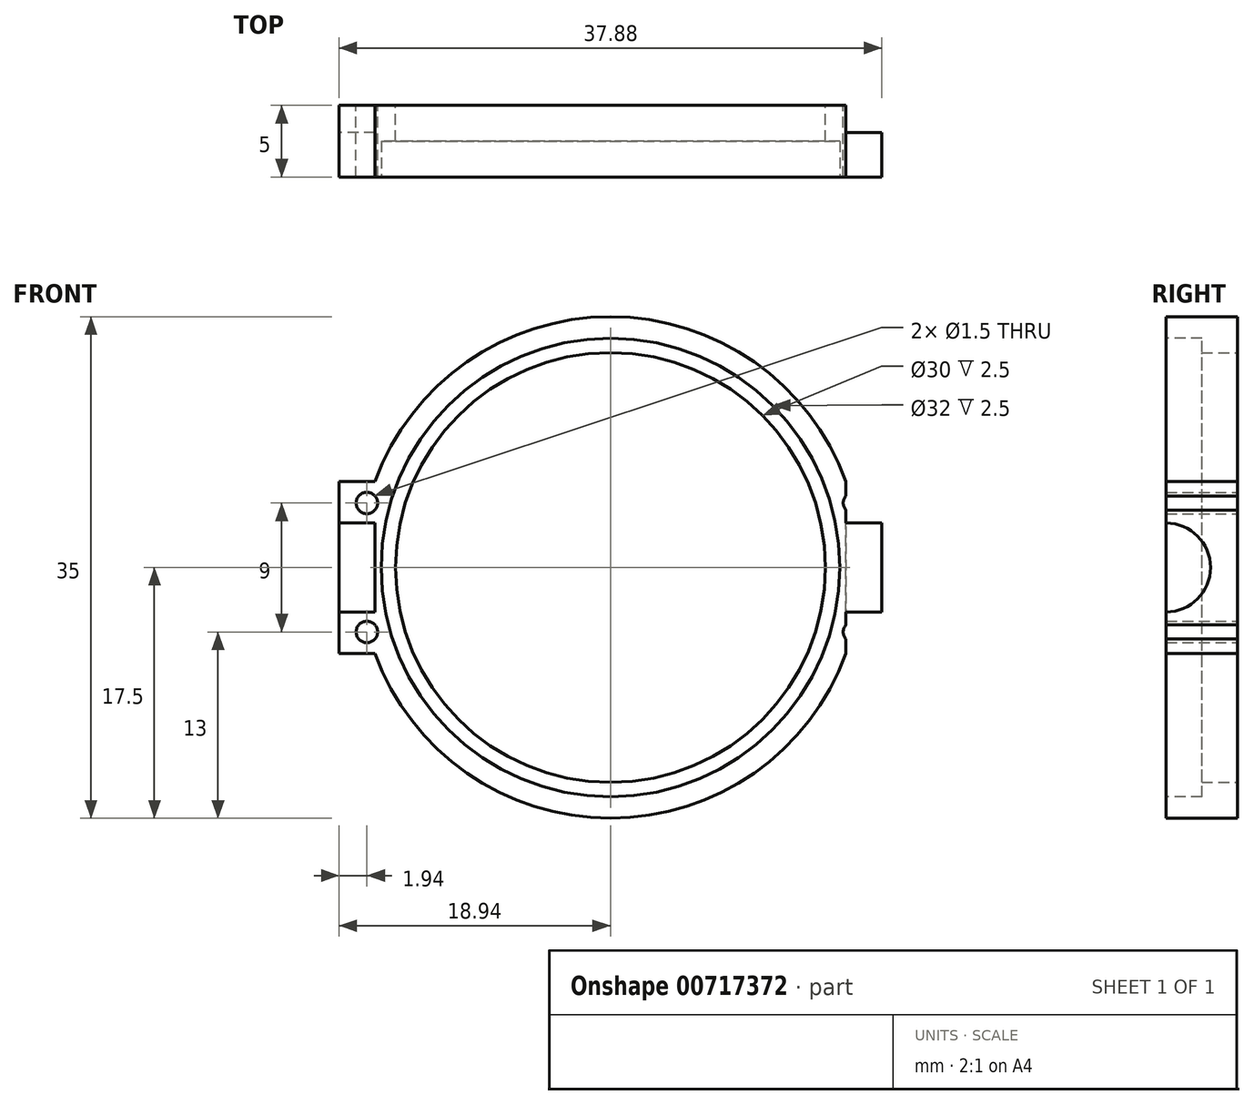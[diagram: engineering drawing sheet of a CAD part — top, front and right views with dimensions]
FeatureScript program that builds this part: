
annotation { "Feature Type Name" : "Feature", "Feature Type Description" : "" }
export const myFeature = defineFeature(function(context is Context, id is Id, definition is map)
    precondition{}
    {
        {
            var Q0;
            Q0=qCreatedBy(makeId("Front.planeOp"),FACE);
            var sketch = newSketch(context, id + "F0", { "sketchPlane" : qUnion([Q0])});
            skCircle(sketch, "E0", {"center": v(0, 0) * mm, "radius": 15 * mm});
            skArc(sketch, "E1", {"start": v(-16.44, -6) * mm, "mid": v(0, -17.5) * mm, "end": v(16.44, -6) * mm});
            skLineSegment(sketch, "E2.bottom", {"start": v(-16.44, 6) * mm, "end": v(-18.94, 6) * mm});
            skLineSegment(sketch, "E2.top", {"start": v(-16.44, -6) * mm, "end": v(-18.94, -6) * mm});
            skLineSegment(sketch, "E2.right", {"start": v(-18.94, 6) * mm, "end": v(-18.94, -6) * mm});
            skLineSegment(sketch, "E3.MirrorCS", {"start": v(16.44, -6) * mm, "end": v(18.94, -6) * mm});
            skLineSegment(sketch, "E4.MirrorCS", {"start": v(16.44, 6) * mm, "end": v(18.94, 6) * mm});
            skLineSegment(sketch, "E5.MirrorCS", {"start": v(18.94, 6) * mm, "end": v(18.94, -6) * mm});
            skArc(sketch, "E6.trimOffspring", {"start": v(16.44, 6) * mm, "mid": v(0, 17.5) * mm, "end": v(-16.44, 6) * mm});
            skSolve(sketch);
        }
        {
            var Q0;
            Q0=makeQuery(id+"F0.imprint","IMPRINT",FACE,{"disambiguationData":[TD([[makeQuery(id+"F0.imprint","IMPRINT",EDGE,{"derivedFrom":sQuery(id+"F0.wireOp",EDGE,"E0")}),-1.0]])]});
            extrude(context, id + "F1", {"entities" : qUnion([Q0]), "depth" : 5 * mm, "offsetDistance" : 25 * mm});
        }
        {
            var Q0;
            Q0=makeQuery(id+"F1.opExtrude","CAP_FACE",FACE,{"disambiguationData":[OSD([sQuery(id+"F0.wireOp",EDGE,"E0"),sQuery(id+"F0.wireOp",EDGE,"E1"),sQuery(id+"F0.wireOp",EDGE,"E2.bottom"),sQuery(id+"F0.wireOp",EDGE,"E2.top"),sQuery(id+"F0.wireOp",EDGE,"E2.right"),sQuery(id+"F0.wireOp",EDGE,"E3.MirrorCS"),sQuery(id+"F0.wireOp",EDGE,"E4.MirrorCS"),sQuery(id+"F0.wireOp",EDGE,"E5.MirrorCS"),sQuery(id+"F0.wireOp",EDGE,"E6.trimOffspring")])],"isStart":false});
            var sketch = newSketch(context, id + "F2", { "sketchPlane" : qUnion([Q0])});
            skCircle(sketch, "E7.0", {"center": v(0, 0) * mm, "radius": 15 * mm});
            skCircle(sketch, "E8.0", {"center": v(0, 0) * mm, "radius": 16 * mm});
            skSolve(sketch);
        }
        {
            var Q0;
            Q0=makeQuery(id+"F2.imprint","IMPRINT",FACE,{"disambiguationData":[TD([[makeQuery(id+"F2.imprint","IMPRINT",EDGE,{"derivedFrom":sQuery(id+"F2.wireOp",EDGE,"E7.0")}),-1.0]])]});
            extrude(context, id + "F3", {"entities" : qUnion([Q0]), "operationType" : NewBodyOperationType.REMOVE, "oppositeDirection" : true, "depth" : 2.5 * mm, "offsetDistance" : 25 * mm});
        }
        {
            var Q0;
            Q0=makeQuery(id+"F1.opExtrude","SWEPT_FACE",FACE,{"disambiguationData":[OSD([sQuery(id+"F0.wireOp",EDGE,"E2.right")])]});
            var sketch = newSketch(context, id + "F4", { "sketchPlane" : qUnion([Q0])});
            skArc(sketch, "E9", {"start": v(5, 3.1) * mm, "mid": v(1.9, 0) * mm, "end": v(5, -3.1) * mm});
            skLineSegment(sketch, "E10", {"start": v(5, 3.1) * mm, "end": v(5, -3.1) * mm});
            skSolve(sketch);
        }
        {
            var Q0;
            Q0=makeQuery(id+"F4.imprint","IMPRINT",FACE,{"disambiguationData":[TD([[makeQuery(id+"F4.imprint","IMPRINT",EDGE,{"derivedFrom":sQuery(id+"F4.wireOp",EDGE,"E9")}),1.0]])]});
            extrude(context, id + "F5", {"entities" : qUnion([Q0]), "operationType" : NewBodyOperationType.REMOVE, "oppositeDirection" : true, "depth" : 2.5 * mm, "offsetDistance" : 25 * mm});
        }
        {
            var Q0;
            Q0=makeQuery(id+"F1.opExtrude","SWEPT_FACE",FACE,{"disambiguationData":[OSD([sQuery(id+"F0.wireOp",EDGE,"E5.MirrorCS")])]});
            var sketch = newSketch(context, id + "F6", { "sketchPlane" : qUnion([Q0])});
            skArc(sketch, "E11", {"start": v(-5, 3.1) * mm, "mid": v(-1.9, 0) * mm, "end": v(-5, -3.1) * mm});
            skLineSegment(sketch, "E12", {"start": v(-5, 3.1) * mm, "end": v(-5, -3.1) * mm});
            skSolve(sketch);
        }
        {
            var Q0;
            Q0=makeQuery(id+"F6.imprint","IMPRINT",FACE,{"disambiguationData":[TD([[makeQuery(id+"F6.imprint","IMPRINT",EDGE,{"derivedFrom":sQuery(id+"F6.wireOp",EDGE,"E11")}),-1.0]])]});
            extrude(context, id + "F7", {"entities" : qUnion([Q0]), "operationType" : NewBodyOperationType.REMOVE, "oppositeDirection" : true, "depth" : 2.5 * mm, "offsetDistance" : 25 * mm});
        }
        {
            var Q0;
            Q0=qCreatedBy(makeId("Front.planeOp"),FACE);
            var sketch = newSketch(context, id + "F8", { "sketchPlane" : qUnion([Q0])});
            skPoint(sketch, "E13", {"position": v(-17, 4.5) * mm});
            skPoint(sketch, "E14", {"position": v(-17, -4.5) * mm});
            skPoint(sketch, "E15.MirrorP", {"position": v(17, 4.5) * mm});
            skPoint(sketch, "E16.MirrorP", {"position": v(17, -4.5) * mm});
            skSolve(sketch);
        }
        {
            var Q0;
            Q0=sQuery(id+"F8.wireOp",VERTEX,"E13");
            var Q1;
            Q1=sQuery(id+"F8.wireOp",VERTEX,"E14");
            var Q2;
            Q2=sQuery(id+"F8.wireOp",VERTEX,"E16.MirrorP");
            var Q3;
            Q3=sQuery(id+"F8.wireOp",VERTEX,"E15.MirrorP");
            var Q4;
            Q4=makeQuery(id+"F1.opExtrude","SWEPT_BODY",BODY,{"disambiguationData":[OSD([sQuery(id+"F0.wireOp",EDGE,"E0"),sQuery(id+"F0.wireOp",EDGE,"E1"),sQuery(id+"F0.wireOp",EDGE,"E2.bottom"),sQuery(id+"F0.wireOp",EDGE,"E2.top"),sQuery(id+"F0.wireOp",EDGE,"E2.right"),sQuery(id+"F0.wireOp",EDGE,"E3.MirrorCS"),sQuery(id+"F0.wireOp",EDGE,"E4.MirrorCS"),sQuery(id+"F0.wireOp",EDGE,"E5.MirrorCS"),sQuery(id+"F0.wireOp",EDGE,"E6.trimOffspring")])]});
            hole(context, id + "F9", {"style" : HoleStyle.SIMPLE, "endStyle" : HoleEndStyle.THROUGH, "oppositeDirection" : true, "holeDiameter" : 1.5 * mm, "majorDiameter" : 5 * mm, "isTappedThrough" : true, "tappedDepth" : 12 * mm, "tapClearance" : 3, "locations" : qUnion([Q0, Q1, Q2, Q3]), "scope" : qUnion([Q4])});
        }
    });
